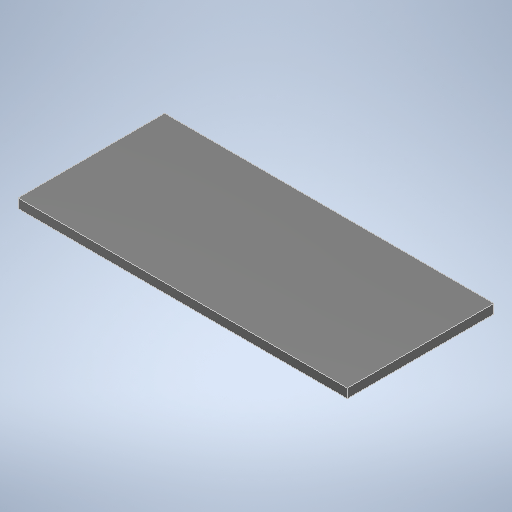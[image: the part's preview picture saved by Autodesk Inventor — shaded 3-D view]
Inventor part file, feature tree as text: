
AUTODESK INVENTOR PART (.ipt)
format: ipt  version: 2025 (Build 290162000, 162)  size: 240,640 bytes
history: native  units: mm
features: extrude x1, sketch x1
ambient origin geometry x8: Origin, YZ Plane, XZ Plane, XY Plane, X Axis, Y Axis, Z Axis, Center Point
bodies: Solid1 (feature_tree)
feature tree (2):
  extrude  "Extrusion1"  Depth=456.0mm
  sketch  "Sketch1"  dims[d0=203.0mm d1=456.0mm d2=12.7mm d3=0.0mm]
